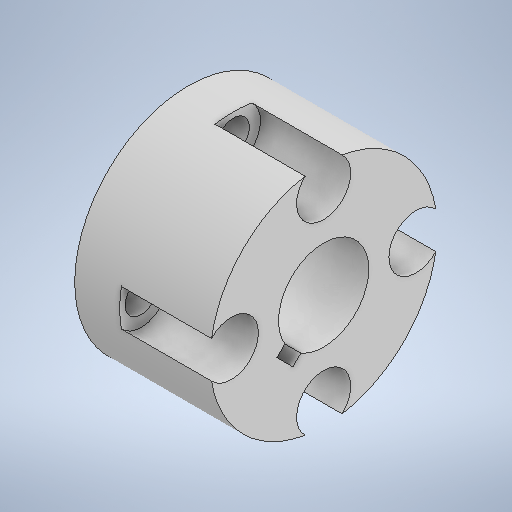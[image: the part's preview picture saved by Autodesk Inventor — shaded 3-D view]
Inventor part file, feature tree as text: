
AUTODESK INVENTOR PART (.ipt)
format: ipt  version: 2025.1 (Build 291241020, 241B)  size: 359,936 bytes
history: native  units: in
note: dims shown in document units (in); Inventor stores cm internally (conversion verified against a paired STEP export)
features: sketch x11, extrude x6, hole x4, projected_geometry x3, plane x1
ambient origin geometry x8: Origin, YZ Plane, XZ Plane, XY Plane, X Axis, Y Axis, Z Axis, Center Point
bodies: Solid1 (feature_tree)
feature tree (25):
  extrude  "Extrusion1"  Depth=0.1575in
  extrude  "Extrusion2"  Depth=0.5118in
  plane  "Work Plane1"
  extrude  "Extrusion4"  Depth=0.5in
  extrude  "Extrusion5"  Depth=0.5906in
  extrude  "Extrusion6"  Depth=0.3937in
  extrude  "Extrusion7"  Depth=0.3in
  hole  "Hole1"  [1 undecoded]
  hole  "Hole2"  [1 undecoded]
  hole  "Hole3"  [1 undecoded]
  hole  "Hole4"  [1 undecoded]
  sketch  "Sketch1"  dims[d0=1.2598in d1=0.1575in]
  sketch  "Sketch Circular Pattern1"  dims[d2=1.0236in d3=0.5118in]
  sketch  "Sketch2"  dims[d4=1.5748in d6=360.0deg d8=0.5in]
  projected_geometry  "Projected Loop1"
  sketch  "Sketch6"  dims[d9=0.1181in d10=0.0in d11=0.5906in]
  projected_geometry  "Projected Loop3"
  sketch  "Sketch7"  dims[d12=0.3937in d13=0.0in d18=0.595in]
  sketch  "Sketch8"  dims[d19=1.0in d20=0.0in d21=0.3in]
  sketch  "Sketch9"  dims[d22=0.3in d23=0.3in]
  projected_geometry  "Projected Loop4"
  sketch  "Sketch10"  dims[d24=0.3in d25=1.0in d26=0.0in]
  sketch  "Sketch11"  dims[d27=0.0625in d28=0.0625in]
  sketch  "Sketch12"  dims[d29=0.0625in d30=0.0625in]
  sketch  "Sketch13"  dims[d31=90.0deg d32=0.0in d33=90.0deg d34=0.125in d35=90.0deg d36=0.5625in d37=0.0in d38=0.238in d39=0.0in d40=0.177in d41=0.75in d42=0.3in d43=0.5in d44=0.5635in d45=1.0in d46=0.8108in d47=0.177in d48=0.75in d49=0.3in d50=0.5in d51=0.5635in d52=1.0in d53=0.8108in d54=0.177in d55=0.75in d56=0.3in d57=0.5in d58=0.5635in d59=1.0in d60=0.8108in d61=0.177in d62=0.75in d63=0.3in d64=0.5in d65=0.5635in d66=1.0in d67=0.8108in]
note: 4 required parameter values undecoded (feature->parameter linkage not recoverable at this tier; creation-order binding heuristic only, values carry confidence <= 0.55)
